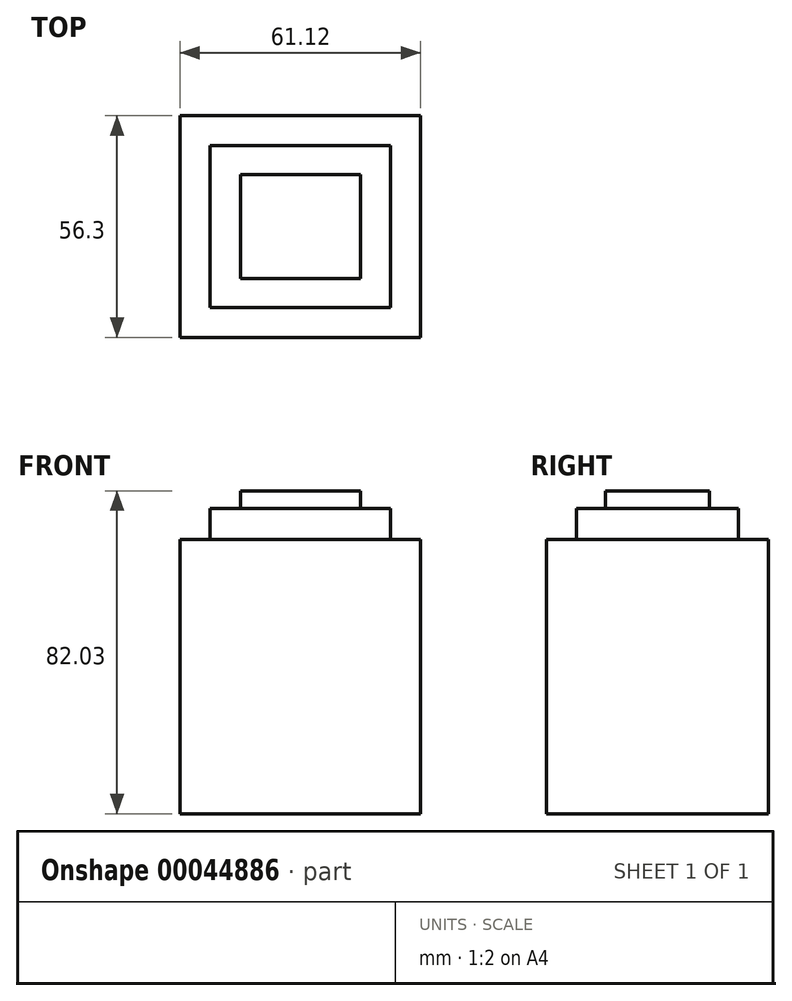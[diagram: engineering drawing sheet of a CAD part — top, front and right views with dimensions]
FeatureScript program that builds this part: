
annotation { "Feature Type Name" : "Feature", "Feature Type Description" : "" }
export const myFeature = defineFeature(function(context is Context, id is Id, definition is map)
    precondition{}
    {
        {
            var Q0;
            Q0=qCreatedBy(makeId("Top.planeOp"),FACE);
            var sketch = newSketch(context, id + "F0", { "sketchPlane" : qUnion([Q0])});
            skLineSegment(sketch, "E0.rect.bottom", {"start": v(30.56, -28.15) * mm, "end": v(-30.56, -28.15) * mm});
            skLineSegment(sketch, "E0.rect.top", {"start": v(30.56, 28.15) * mm, "end": v(-30.56, 28.15) * mm});
            skLineSegment(sketch, "E0.rect.left", {"start": v(30.56, -28.15) * mm, "end": v(30.56, 28.15) * mm});
            skLineSegment(sketch, "E0.rect.right", {"start": v(-30.56, -28.15) * mm, "end": v(-30.56, 28.15) * mm});
            skPoint(sketch, "E0.rect.middle", {"position": v(0, 0) * mm});
            skSolve(sketch);
        }
        {
            var Q0;
            Q0 = qSketchRegion(id + "F0", true);
            extrude(context, id + "F1", {"entities" : qUnion([Q0]), "depth" : 37.52 * mm, "hasSecondDirection" : true, "secondDirectionOppositeDirection" : true, "secondDirectionDepth" : 32.22 * mm});
        }
        {
            var Q0;
            Q0=makeQuery(id+"F1.opExtrude","CAP_FACE",FACE,{"disambiguationData":[OSD([sQuery(id+"F0.wireOp",EDGE,"E0.rect.bottom"),sQuery(id+"F0.wireOp",EDGE,"E0.rect.top"),sQuery(id+"F0.wireOp",EDGE,"E0.rect.left"),sQuery(id+"F0.wireOp",EDGE,"E0.rect.right")])],"isStart":false});
            var sketch = newSketch(context, id + "F2", { "sketchPlane" : qUnion([Q0])});
            skLineSegment(sketch, "E1.rect.bottom", {"start": v(-22.87, -20.55) * mm, "end": v(22.87, -20.55) * mm});
            skLineSegment(sketch, "E1.rect.top", {"start": v(-22.87, 20.55) * mm, "end": v(22.87, 20.55) * mm});
            skLineSegment(sketch, "E1.rect.left", {"start": v(-22.87, -20.55) * mm, "end": v(-22.87, 20.55) * mm});
            skLineSegment(sketch, "E1.rect.right", {"start": v(22.87, -20.55) * mm, "end": v(22.87, 20.55) * mm});
            skPoint(sketch, "E1.rect.middle", {"position": v(0, 0) * mm});
            skSolve(sketch);
        }
        {
            var Q0;
            Q0 = qSketchRegion(id + "F2", true);
            extrude(context, id + "F3", {"entities" : qUnion([Q0]), "operationType" : NewBodyOperationType.ADD, "depth" : 7.85 * mm});
        }
        {
            var Q0;
            Q0=makeQuery(id+"F3.opExtrude","CAP_FACE",FACE,{"disambiguationData":[OSD([sQuery(id+"F2.wireOp",EDGE,"E1.rect.bottom"),sQuery(id+"F2.wireOp",EDGE,"E1.rect.top"),sQuery(id+"F2.wireOp",EDGE,"E1.rect.left"),sQuery(id+"F2.wireOp",EDGE,"E1.rect.right")])],"isStart":false});
            var sketch = newSketch(context, id + "F4", { "sketchPlane" : qUnion([Q0])});
            skLineSegment(sketch, "E2.rect.bottom", {"start": v(15.25, -13.19) * mm, "end": v(-15.25, -13.19) * mm});
            skLineSegment(sketch, "E2.rect.top", {"start": v(15.25, 13.19) * mm, "end": v(-15.25, 13.19) * mm});
            skLineSegment(sketch, "E2.rect.left", {"start": v(15.25, -13.19) * mm, "end": v(15.25, 13.19) * mm});
            skLineSegment(sketch, "E2.rect.right", {"start": v(-15.25, -13.19) * mm, "end": v(-15.25, 13.19) * mm});
            skPoint(sketch, "E2.rect.middle", {"position": v(0, 0) * mm});
            skSolve(sketch);
        }
        {
            var Q0;
            Q0 = qSketchRegion(id + "F4", true);
            extrude(context, id + "F5", {"entities" : qUnion([Q0]), "operationType" : NewBodyOperationType.ADD, "depth" : 4.44 * mm});
        }
    });
